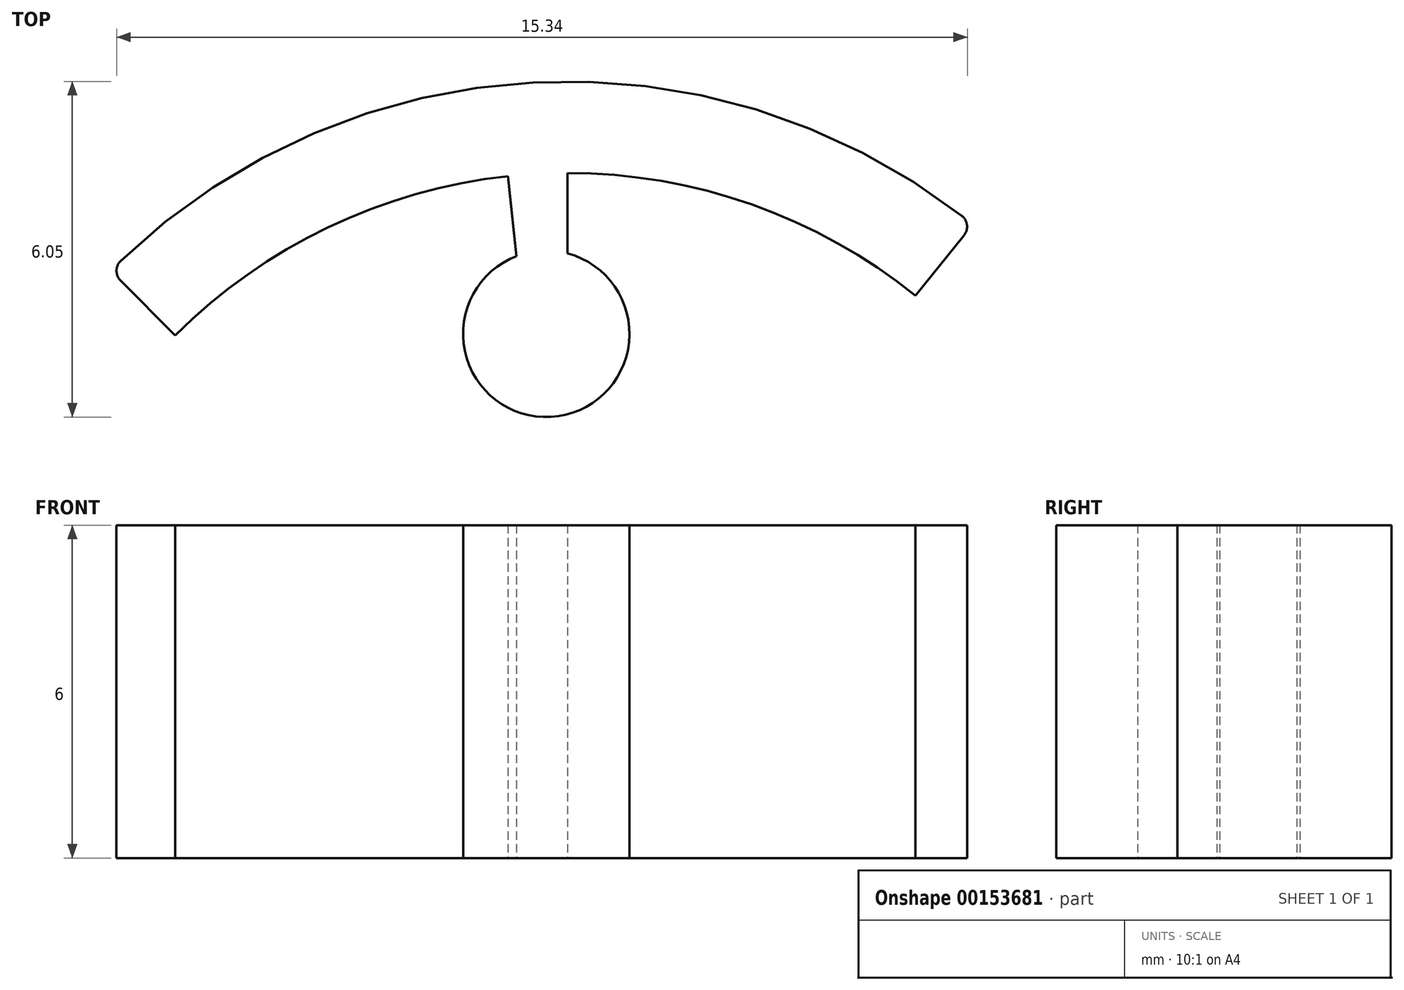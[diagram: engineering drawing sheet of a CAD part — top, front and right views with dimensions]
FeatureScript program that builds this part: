
annotation { "Feature Type Name" : "Feature", "Feature Type Description" : "" }
export const myFeature = defineFeature(function(context is Context, id is Id, definition is map)
    precondition{}
    {
        {
            var Q0;
            Q0=qCreatedBy(makeId("Top.planeOp"),FACE);
            var sketch = newSketch(context, id + "F0", { "sketchPlane" : qUnion([Q0])});
            skArc(sketch, "E0", {"start": v(0, 10) * mm, "mid": v(-0.54, 9.99) * mm, "end": v(-1.07, 9.94) * mm, "construction": true});
            skLineSegment(sketch, "E1", {"start": v(-8.06, 8.06) * mm, "end": v(-7.07, 7.07) * mm});
            skArc(sketch, "E2", {"start": v(0.26, 11.65) * mm, "mid": v(-4.22, 10.86) * mm, "end": v(-8.06, 8.42) * mm});
            skArc(sketch, "E3", {"start": v(-1.07, 9.94) * mm, "mid": v(-4.32, 9.02) * mm, "end": v(-7.07, 7.07) * mm});
            skPoint(sketch, "E4.visualSharp", {"position": v(-8.24, 8.24) * mm});
            skArc(sketch, "E4.filletArc", {"start": v(-8.06, 8.42) * mm, "mid": v(-8.13, 8.24) * mm, "end": v(-8.06, 8.06) * mm});
            skPoint(sketch, "E5.visualSharp", {"position": v(-1.25, 11.58) * mm});
            skArc(sketch, "E6", {"start": v(0.26, 11.65) * mm, "mid": v(3.87, 10.99) * mm, "end": v(7.1, 9.23) * mm});
            skArc(sketch, "E7", {"start": v(0, 10) * mm, "mid": v(3.33, 9.43) * mm, "end": v(6.27, 7.79) * mm});
            skLineSegment(sketch, "E8", {"start": v(7.15, 8.88) * mm, "end": v(6.27, 7.79) * mm});
            skPoint(sketch, "E9.visualSharp", {"position": v(0, 11.65) * mm});
            skPoint(sketch, "E10.visualSharp", {"position": v(7.3, 9.07) * mm});
            skArc(sketch, "E10.filletArc", {"start": v(7.15, 8.88) * mm, "mid": v(7.2, 9.06) * mm, "end": v(7.1, 9.23) * mm});
            skLineSegment(sketch, "E11", {"start": v(-1.07, 9.94) * mm, "end": v(-0.92, 8.5) * mm});
            skLineSegment(sketch, "E12", {"start": v(0, 10) * mm, "end": v(0, 8.55) * mm});
            skArc(sketch, "E13", {"start": v(-0.92, 8.5) * mm, "mid": v(-0.3, 5.6) * mm, "end": v(0, 8.55) * mm});
            skLineSegment(sketch, "E14", {"start": v(-0.92, 8.5) * mm, "end": v(0, 8.55) * mm, "construction": true});
            skLineSegment(sketch, "E15", {"start": v(-0.46, 8.53) * mm, "end": v(-0.38, 7.1) * mm, "construction": true});
            skSolve(sketch);
        }
        {
            var Q0;
            Q0=qSketchRegion(id+"F0",true);
            extrude(context, id + "F1", {"entities" : qUnion([Q0]), "depth" : 6 * mm});
        }
    });
